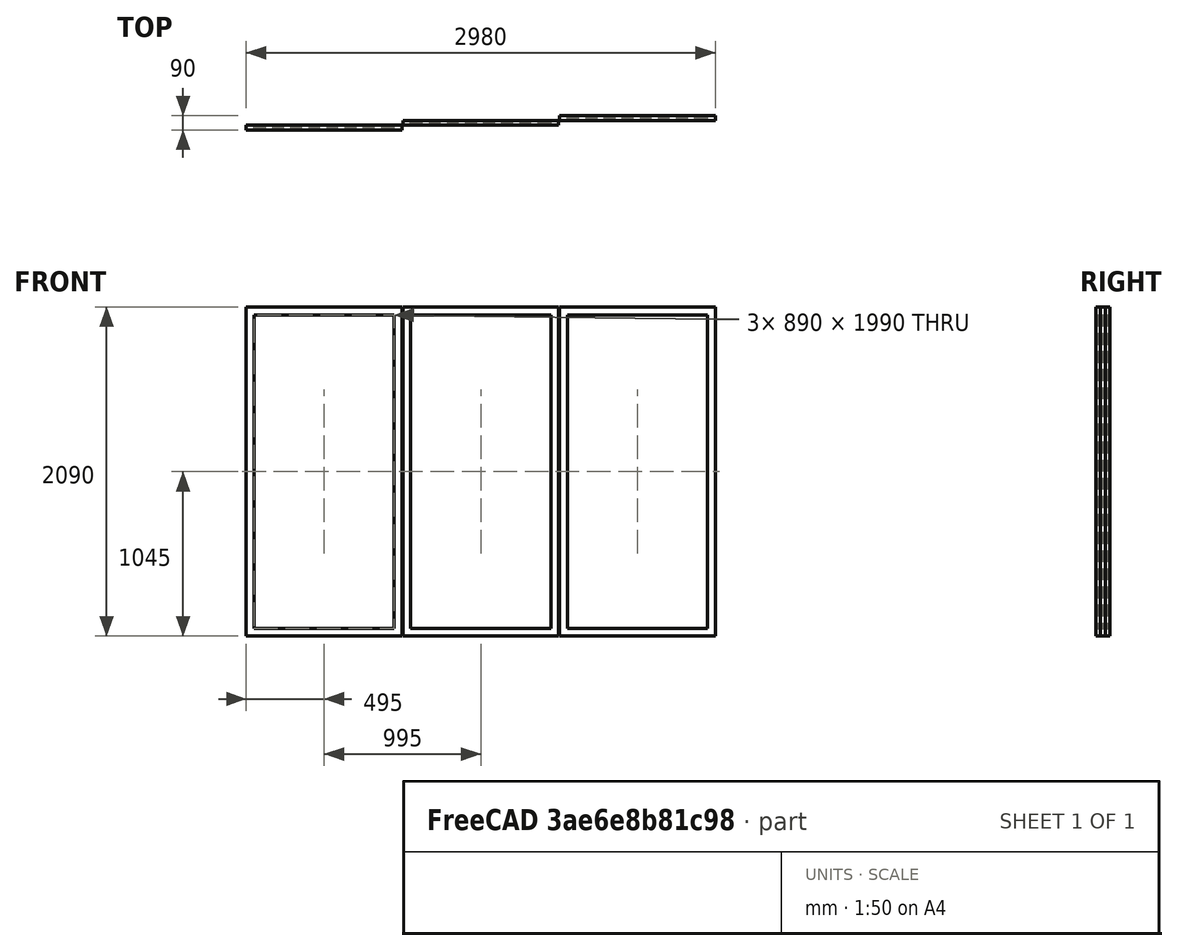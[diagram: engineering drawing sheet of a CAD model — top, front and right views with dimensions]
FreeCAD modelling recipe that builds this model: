
FCSTD DOCUMENT  (FreeCAD 0.20R29410 (Git))
Label: Porta de correr 3 folhas
License: All rights reserved
objects: Sketcher::SketchObject×1, Part::FeaturePython×1
note: 2 computed .brp shape members not serialized (recipe doc carries the construction recipe); baked Part::Feature solids carry a one-line shape summary decoded from their .brp

FEATURE [Sketcher::SketchObject] Sketch
  FullyConstrained = true
  Placement = pos=(0,0,0) rot=(1,0,0;1.5708rad)
  expr: Constraints[17] = .Constraints.altura - 100mm - 10mm
  expr: Constraints[18] = .Constraints.comprimento / 3 - 100mm - 10mm
  expr: Constraints[29] = .Constraints.altura - 10mm
  expr: Constraints[30] = .Constraints.comprimento / 3 - 10mm
  sketch-geometry (28):
    g0: LineSegment StartX=0 StartY=0 StartZ=0 EndX=3000 EndY=0 EndZ=0
    g1: LineSegment StartX=3000 StartY=0 StartZ=0 EndX=3000 EndY=2100 EndZ=0
    g2: LineSegment StartX=3000 StartY=2100 StartZ=0 EndX=0 EndY=2100 EndZ=0
    g3: LineSegment StartX=0 StartY=2100 StartZ=0 EndX=0 EndY=0 EndZ=0
    g4: LineSegment StartX=55 StartY=2045 StartZ=0 EndX=945 EndY=2045 EndZ=0
    g5: LineSegment StartX=945 StartY=2045 StartZ=0 EndX=945 EndY=55 EndZ=0
    g6: LineSegment StartX=945 StartY=55 StartZ=0 EndX=55 EndY=55 EndZ=0
    g7: LineSegment StartX=55 StartY=55 StartZ=0 EndX=55 EndY=2045 EndZ=0
    g8: LineSegment StartX=5 StartY=2095 StartZ=0 EndX=995 EndY=2095 EndZ=0
    g9: LineSegment StartX=995 StartY=2095 StartZ=0 EndX=995 EndY=5 EndZ=0
    g10: LineSegment StartX=995 StartY=5 StartZ=0 EndX=5 EndY=5 EndZ=0
    g11: LineSegment StartX=5 StartY=5 StartZ=0 EndX=5 EndY=2095 EndZ=0
    g12: LineSegment StartX=1000 StartY=2095 StartZ=0 EndX=1990 EndY=2095 EndZ=0
    g13: LineSegment StartX=1990 StartY=2095 StartZ=0 EndX=1990 EndY=5 EndZ=0
    g14: LineSegment StartX=1990 StartY=5 StartZ=0 EndX=1000 EndY=5 EndZ=0
    g15: LineSegment StartX=1000 StartY=5 StartZ=0 EndX=1000 EndY=2095 EndZ=0
    g16: LineSegment StartX=1995 StartY=2095 StartZ=0 EndX=2985 EndY=2095 EndZ=0
    g17: LineSegment StartX=2985 StartY=2095 StartZ=0 EndX=2985 EndY=5 EndZ=0
    g18: LineSegment StartX=2985 StartY=5 StartZ=0 EndX=1995 EndY=5 EndZ=0
    g19: LineSegment StartX=1995 StartY=5 StartZ=0 EndX=1995 EndY=2095 EndZ=0
    g20: LineSegment StartX=1050 StartY=2045 StartZ=0 EndX=1940 EndY=2045 EndZ=0
    g21: LineSegment StartX=1940 StartY=2045 StartZ=0 EndX=1940 EndY=55 EndZ=0
    g22: LineSegment StartX=1940 StartY=55 StartZ=0 EndX=1050 EndY=55 EndZ=0
    g23: LineSegment StartX=1050 StartY=55 StartZ=0 EndX=1050 EndY=2045 EndZ=0
    g24: LineSegment StartX=2045 StartY=2045 StartZ=0 EndX=2935 EndY=2045 EndZ=0
    g25: LineSegment StartX=2935 StartY=2045 StartZ=0 EndX=2935 EndY=55 EndZ=0
    g26: LineSegment StartX=2935 StartY=55 StartZ=0 EndX=2045 EndY=55 EndZ=0
    g27: LineSegment StartX=2045 StartY=55 StartZ=0 EndX=2045 EndY=2045 EndZ=0
  constraints (83):
    c: Coincident(g1,g2)
    c: Coincident(g2,g3)
    c: Horizontal(g0)
    c: Horizontal(g2)
    c: Vertical(g1)
    c: Vertical(g3)
    c: Coincident(g0,g-1)
    c: DistanceX(g2,g2) = 3000  'comprimento'
    c: DistanceY(g1,g1) = 2100  'altura'
    c: Coincident(g4,g5)
    c: Coincident(g5,g6)
    c: Coincident(g6,g7)
    c: Coincident(g7,g4)
    c: Horizontal(g4)
    c: Horizontal(g6)
    c: Vertical(g5)
    c: Vertical(g7)
    c: DistanceY(g7,g7) = 1990
    c: DistanceX(g4,g4) = 890
    c: Coincident(g0,g1)
    c: Coincident(g0,g3)
    c: Coincident(g8,g9)
    c: Coincident(g9,g10)
    c: Coincident(g10,g11)
    c: Coincident(g11,g8)
    c: Horizontal(g8)
    c: Horizontal(g10)
    c: Vertical(g9)
    c: Vertical(g11)
    c: DistanceY(g9,g9) = 2090
    c: DistanceX(g8,g8) = 990
    c: Coincident(g12,g13)
    c: Coincident(g13,g14)
    c: Coincident(g14,g15)
    c: Coincident(g15,g12)
    c: Horizontal(g12)
    c: Horizontal(g14)
    c: Vertical(g13)
    c: Vertical(g15)
    c: Equal(g9,g13) = 2090
    c: Equal(g8,g12) = 990
    c: Coincident(g16,g17)
    c: Coincident(g17,g18)
    c: Coincident(g18,g19)
    c: Coincident(g19,g16)
    c: Horizontal(g16)
    c: Horizontal(g18)
    c: Vertical(g17)
    c: Vertical(g19)
    c: Equal(g9,g17) = 2090
    c: Equal(g8,g16) = 990
    c: DistanceX(g9,g14) = 5
    c: DistanceX(g13,g18) = 5
    c: DistanceY(g14,g9) = 0
    c: DistanceY(g13,g18) = 0
    c: DistanceX(g0,g10) = 5
    c: DistanceY(g0,g10) = 5
    c: Coincident(g20,g21)
    c: Coincident(g21,g22)
    c: Coincident(g22,g23)
    c: Coincident(g23,g20)
    c: Horizontal(g20)
    c: Horizontal(g22)
    c: Vertical(g21)
    c: Vertical(g23)
    c: Equal(g7,g23) = 2000
    c: Equal(g4,g20) = 900
    c: Coincident(g24,g25)
    c: Coincident(g25,g26)
    c: Coincident(g26,g27)
    c: Coincident(g27,g24)
    c: Horizontal(g24)
    c: Horizontal(g26)
    c: Vertical(g25)
    c: Vertical(g27)
    c: Equal(g7,g27) = 2000
    c: Equal(g4,g24) = 900
    c: DistanceX(g10,g6) = 50
    c: DistanceY(g10,g6) = 50
    c: DistanceX(g14,g22) = 50
    c: DistanceY(g14,g22) = 50
    c: DistanceY(g18,g26) = 50
    c: DistanceX(g18,g26) = 50
FEATURE [Part::FeaturePython] Window  label="Janela"  # Arch/BIM 41 (typed FeaturePython)
  Area = 0
  Base = -> Sketch
  Frame = 0
  Height = 0
  HoleDepth = 0
  HoleWire = 1
  HorizontalArea = 0
  IfcData = attributes={"GlobalId": {"name": "GlobalId", "type": "IfcGloballyUniqueId", "is_enum": false, "enum_values": []}, "Description": {"... (+1928 chars omitted),+1 more (map truncated)
  IfcType = 41
  LouvreSpacing = 0
  LouvreWidth = 0
  MoveBase = false
  MoveWithHost = true
  Normal = (0,1,-2e-16)
  Opening = 0
  OperationType = 0
  OverallHeight = 0
  OverallWidth = 0
  PerimeterLength = 0
  PredefinedType = 0
  Preset = 0
  SymbolElevation = false
  SymbolPlan = false
  VerticalArea = 0
  Width = 0
  WindowParts = frame1 | Frame | Wire1,Wire2 | 30.0 | 0.0 | Frame2 | Frame | Wire3,Wire5 | 30.0 | 30.0 | Frame3 | Frame | Wire4,Wire6 | 30.0 | 60.0 | vidro1 | Glass panel | Wire1 | 5.0 | 15.0 | vidro2 | Glass panel | Wire5 | 5.0 | 45.0 | vidro3 | Glass panel | Wire6 | 5.0 | 75.0
  expr: OverallHeight = .Height.Value
  expr: OverallWidth = .Width.Value
